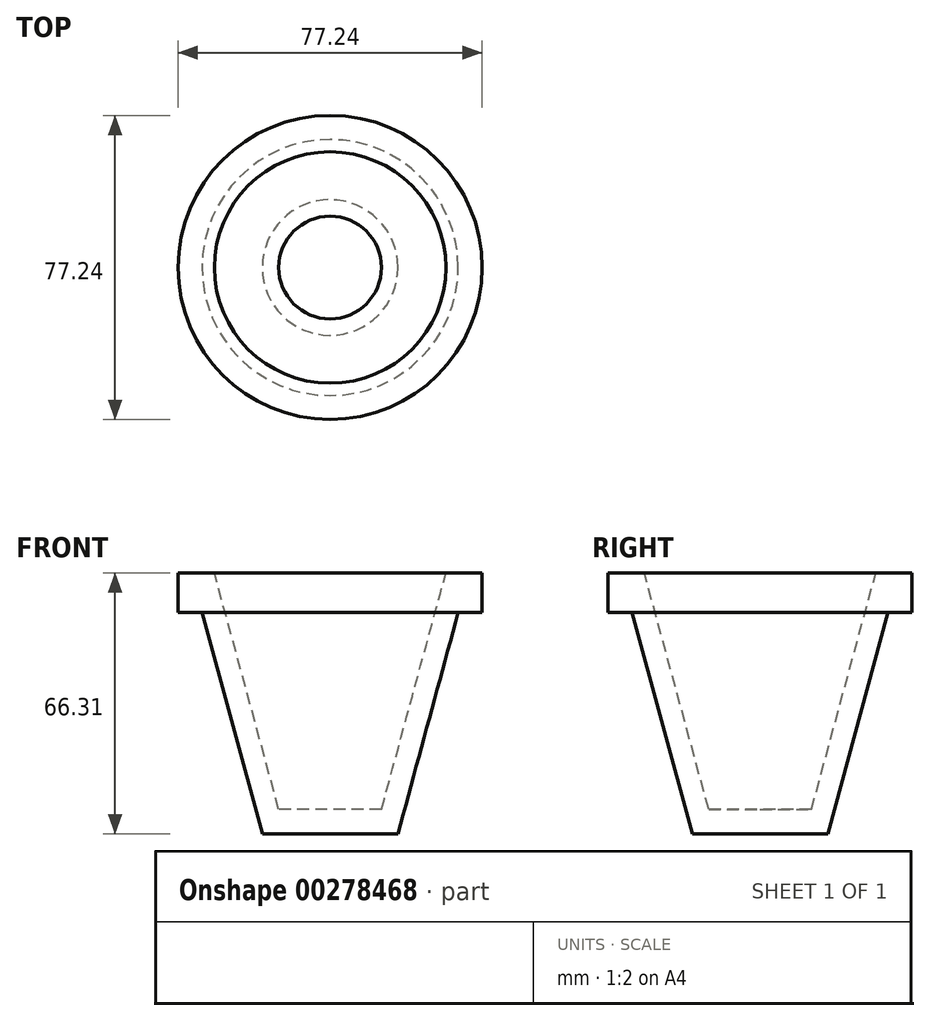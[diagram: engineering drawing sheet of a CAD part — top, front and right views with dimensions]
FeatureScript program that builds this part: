
annotation { "Feature Type Name" : "Feature", "Feature Type Description" : "" }
export const myFeature = defineFeature(function(context is Context, id is Id, definition is map)
    precondition{}
    {
        {
            var Q0;
            Q0=qCreatedBy(makeId("Front.planeOp"),FACE);
            var sketch = newSketch(context, id + "F0", { "sketchPlane" : qUnion([Q0])});
            skLineSegment(sketch, "E0", {"start": v(0, -28.3) * mm, "end": v(-17.22, -28.3) * mm});
            skLineSegment(sketch, "E1", {"start": v(-17.22, -28.3) * mm, "end": v(-32.53, 27.94) * mm});
            skLineSegment(sketch, "E2", {"start": v(-32.53, 27.94) * mm, "end": v(-38.62, 27.94) * mm});
            skLineSegment(sketch, "E3", {"start": v(-38.62, 27.94) * mm, "end": v(-38.62, 38.01) * mm});
            skLineSegment(sketch, "E4", {"start": v(-38.62, 38.01) * mm, "end": v(-29.4, 38.01) * mm});
            skLineSegment(sketch, "E5", {"start": v(-29.4, 38.01) * mm, "end": v(-13.06, -22.05) * mm});
            skLineSegment(sketch, "E6", {"start": v(-13.06, -22.05) * mm, "end": v(0, -22.05) * mm});
            skLineSegment(sketch, "E7", {"start": v(0, -22.05) * mm, "end": v(0, -28.3) * mm});
            skSolve(sketch);
        }
        {
            var Q0;
            Q0 = qSketchRegion(id + "F0", true);
            var Q1;
            Q1=sQuery(id+"F0.wireOp",EDGE,"E7");
            revolve(context, id + "F1", {"entities" : qUnion([Q0]), "axis" : qUnion([Q1]), "revolveType" : RevolveType.FULL});
        }
    });
